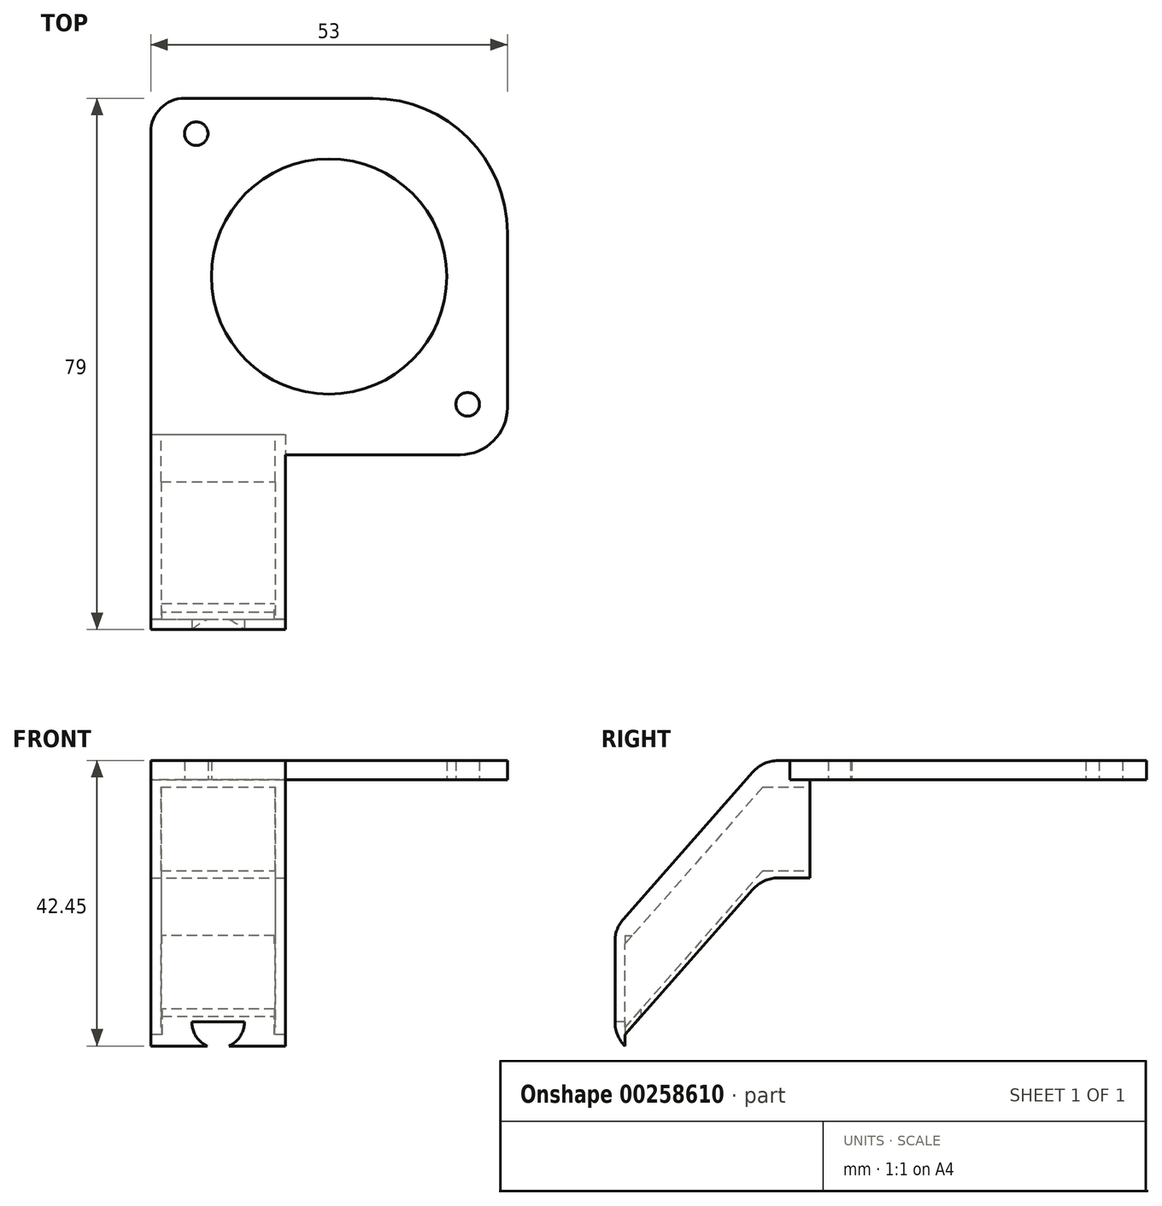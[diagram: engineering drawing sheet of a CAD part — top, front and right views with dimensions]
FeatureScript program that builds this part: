
annotation { "Feature Type Name" : "Feature", "Feature Type Description" : "" }
export const myFeature = defineFeature(function(context is Context, id is Id, definition is map)
    precondition{}
    {
        {
            var Q0;
            Q0=qCreatedBy(makeId("Top.planeOp"),FACE);
            var sketch = newSketch(context, id + "F0", { "sketchPlane" : qUnion([Q0])});
            skCircle(sketch, "E0", {"center": v(0, 0) * mm, "radius": 17.5 * mm});
            skLineSegment(sketch, "E1.bottom", {"start": v(19.5, -26.5) * mm, "end": v(-6.5, -26.5) * mm});
            skLineSegment(sketch, "E1.top", {"start": v(6.5, 26.5) * mm, "end": v(-21.5, 26.5) * mm});
            skLineSegment(sketch, "E1.left", {"start": v(26.5, -19.5) * mm, "end": v(26.5, 6.5) * mm});
            skLineSegment(sketch, "E1.right", {"start": v(-26.5, -26.5) * mm, "end": v(-26.5, 21.5) * mm});
            skCircle(sketch, "E2", {"center": v(-19.75, 21.25) * mm, "radius": 1.75 * mm});
            skCircle(sketch, "E3", {"center": v(20.6, -19.01) * mm, "radius": 1.75 * mm});
            skPoint(sketch, "E4.visualSharp", {"position": v(-26.5, 26.5) * mm});
            skArc(sketch, "E4.filletArc", {"start": v(-21.5, 26.5) * mm, "mid": v(-25.04, 25.04) * mm, "end": v(-26.5, 21.5) * mm});
            skPoint(sketch, "E5.visualSharp", {"position": v(26.5, -26.5) * mm});
            skArc(sketch, "E5.filletArc", {"start": v(19.5, -26.5) * mm, "mid": v(24.45, -24.45) * mm, "end": v(26.5, -19.5) * mm});
            skPoint(sketch, "E6.visualSharp", {"position": v(26.5, 26.5) * mm});
            skArc(sketch, "E6.filletArc", {"start": v(26.5, 6.5) * mm, "mid": v(20.64, 20.64) * mm, "end": v(6.5, 26.5) * mm});
            skLineSegment(sketch, "E7.top", {"start": v(-26.5, -30.5) * mm, "end": v(-6.5, -30.5) * mm});
            skLineSegment(sketch, "E7.left", {"start": v(-26.5, -26.5) * mm, "end": v(-26.5, -30.5) * mm});
            skLineSegment(sketch, "E7.right", {"start": v(-6.5, -26.5) * mm, "end": v(-6.5, -30.5) * mm});
            skSolve(sketch);
        }
        {
            var Q0;
            Q0=makeQuery(id+"F0.imprint","IMPRINT",FACE,{"disambiguationData":[TD([[makeQuery(id+"F0.imprint","IMPRINT",EDGE,{"derivedFrom":sQuery(id+"F0.wireOp",EDGE,"E0")}),-1.0]])]});
            extrude(context, id + "F1", {"entities" : qUnion([Q0]), "depth" : 2.85 * mm});
        }
        {
            var Q0;
            Q0=makeQuery(id+"F1.opExtrude","CAP_FACE",FACE,{"disambiguationData":[OSD([sQuery(id+"F0.wireOp",EDGE,"E0"),sQuery(id+"F0.wireOp",EDGE,"E1.bottom"),sQuery(id+"F0.wireOp",EDGE,"E1.top"),sQuery(id+"F0.wireOp",EDGE,"E1.left"),sQuery(id+"F0.wireOp",EDGE,"E1.right"),sQuery(id+"F0.wireOp",EDGE,"E2"),sQuery(id+"F0.wireOp",EDGE,"E3"),sQuery(id+"F0.wireOp",EDGE,"E4.filletArc"),sQuery(id+"F0.wireOp",EDGE,"E5.filletArc"),sQuery(id+"F0.wireOp",EDGE,"E6.filletArc"),sQuery(id+"F0.wireOp",EDGE,"E7.top"),sQuery(id+"F0.wireOp",EDGE,"E7.left"),sQuery(id+"F0.wireOp",EDGE,"E7.right")])],"isStart":true});
            var sketch = newSketch(context, id + "F2", { "sketchPlane" : qUnion([Q0])});
            skLineSegment(sketch, "E8.bottom", {"start": v(-26.5, 30.5) * mm, "end": v(-6.5, 30.5) * mm});
            skLineSegment(sketch, "E8.top", {"start": v(-26.5, 26.5) * mm, "end": v(-6.5, 26.5) * mm});
            skLineSegment(sketch, "E8.left", {"start": v(-26.5, 30.5) * mm, "end": v(-26.5, 26.5) * mm});
            skLineSegment(sketch, "E8.right", {"start": v(-6.5, 30.5) * mm, "end": v(-6.5, 26.5) * mm});
            skSolve(sketch);
        }
        {
            var Q0;
            Q0=makeQuery(id+"F2.imprint","IMPRINT",FACE,{"disambiguationData":[TD([[makeQuery(id+"F2.imprint","IMPRINT",EDGE,{"derivedFrom":sQuery(id+"F2.wireOp",EDGE,"E8.bottom")}),-1.0]])]});
            extrude(context, id + "F3", {"entities" : qUnion([Q0]), "operationType" : NewBodyOperationType.ADD, "depth" : 14.6 * mm});
        }
        {
            var Q0;
            Q0=makeQuery(id+"F3.opExtrude","SWEPT_FACE",FACE,{"disambiguationData":[OSD([sQuery(id+"F2.wireOp",EDGE,"E8.top")])]});
            var sketch = newSketch(context, id + "F4", { "sketchPlane" : qUnion([Q0])});
            skLineSegment(sketch, "E9", {"start": v(26.5, -14.6) * mm, "end": v(6.5, 0) * mm, "construction": true});
            skLineSegment(sketch, "E10", {"start": v(6.5, -14.6) * mm, "end": v(26.5, 0) * mm, "construction": true});
            skLineSegment(sketch, "E11.bottom", {"start": v(25, -13.5) * mm, "end": v(8, -13.5) * mm});
            skLineSegment(sketch, "E11.top", {"start": v(25, -1.1) * mm, "end": v(8, -1.1) * mm});
            skLineSegment(sketch, "E11.left", {"start": v(25, -13.5) * mm, "end": v(25, -1.1) * mm});
            skLineSegment(sketch, "E11.right", {"start": v(8, -13.5) * mm, "end": v(8, -1.1) * mm});
            skPoint(sketch, "E11.middle", {"position": v(16.5, -7.3) * mm});
            skSolve(sketch);
        }
        {
            var Q0;
            Q0=makeQuery(id+"F4.imprint","IMPRINT",FACE,{"disambiguationData":[TD([[makeQuery(id+"F4.imprint","IMPRINT",EDGE,{"derivedFrom":sQuery(id+"F4.wireOp",EDGE,"E11.bottom")}),-1.0]])]});
            extrude(context, id + "F5", {"entities" : qUnion([Q0]), "operationType" : NewBodyOperationType.REMOVE, "oppositeDirection" : true, "depth" : 25 * mm});
        }
        {
            var Q0;
            Q0=makeQuery(id+"F3.boolean.opBoolean","MERGE",FACE,{"derivedFrom":[makeQuery(id+"F1.opExtrude","SWEPT_FACE",FACE,{"disambiguationData":[OSD([sQuery(id+"F0.wireOp",EDGE,"E7.right")])]}),makeQuery(id+"F3.opExtrude","SWEPT_FACE",FACE,{"disambiguationData":[OSD([sQuery(id+"F2.wireOp",EDGE,"E8.right")])]})]});
            cPlane(context, id + "F6", {"entities" : qUnion([Q0]), "cplaneType" : CPlaneType.OFFSET, "offset" : 10 * mm, "oppositeDirection" : true, "width" : 150 * mm, "height" : 150 * mm});
        }
        {
            var Q0;
            Q0=qCreatedBy(id+"F6.planeOp",FACE);
            var sketch = newSketch(context, id + "F7", { "sketchPlane" : qUnion([Q0])});
            skLineSegment(sketch, "E12", {"start": v(-30.58, -0.14) * mm, "end": v(-52.58, -0.14) * mm, "construction": true});
            skLineSegment(sketch, "E13", {"start": v(-52.58, -0.14) * mm, "end": v(-52.58, -25.14) * mm, "construction": true});
            skLineSegment(sketch, "E14", {"start": v(-30.58, -0.14) * mm, "end": v(-52.58, -25.14) * mm});
            skSolve(sketch);
        }
        {
            var Q0;
            Q0=makeQuery(id+"F3.boolean.opBoolean","MERGE",FACE,{"derivedFrom":[makeQuery(id+"F1.opExtrude","SWEPT_FACE",FACE,{"disambiguationData":[OSD([sQuery(id+"F0.wireOp",EDGE,"E7.top")])]}),makeQuery(id+"F3.opExtrude","SWEPT_FACE",FACE,{"disambiguationData":[OSD([sQuery(id+"F2.wireOp",EDGE,"E8.bottom")])]})]});
            var Q1;
            Q1=sQuery(id+"F7.wireOp",EDGE,"E14");
            sweep(context, id + "F8", {"operationType" : NewBodyOperationType.ADD, "profiles" : qUnion([Q0]), "path" : qUnion([Q1])});
        }
        {
            var Q0;
            Q0=makeQuery(id+"F8.opSweep","CAP_FACE",FACE,{"disambiguationData":[OSD([sQuery(id+"F0.wireOp",EDGE,"E7.top"),sQuery(id+"F2.wireOp",EDGE,"E8.bottom"),sQuery(id+"F7.wireOp",VERTEX,"E14.end")])],"isStart":false});
            var sketch = newSketch(context, id + "F9", { "sketchPlane" : qUnion([Q0])});
            skLineSegment(sketch, "E15.bottom", {"start": v(-26.5, -22.15) * mm, "end": v(-6.5, -22.15) * mm});
            skLineSegment(sketch, "E15.top", {"start": v(-26.5, -39.6) * mm, "end": v(-6.5, -39.6) * mm});
            skLineSegment(sketch, "E15.left", {"start": v(-26.5, -22.15) * mm, "end": v(-26.5, -39.6) * mm});
            skLineSegment(sketch, "E15.right", {"start": v(-6.5, -22.15) * mm, "end": v(-6.5, -39.6) * mm});
            skSolve(sketch);
        }
        {
            var Q0;
            Q0 = qSketchRegion(id + "F9", true);
            extrude(context, id + "F10", {"entities" : qUnion([Q0]), "operationType" : NewBodyOperationType.ADD, "oppositeDirection" : true, "depth" : 1.5 * mm});
        }
        {
            var Q0;
            Q0=makeQuery(id+"F10.opExtrude","SWEPT_FACE",FACE,{"disambiguationData":[OSD([sQuery(id+"F9.wireOp",EDGE,"E15.top")])]});
            var sketch = newSketch(context, id + "F11", { "sketchPlane" : qUnion([Q0])});
            skLineSegment(sketch, "E16.bottom", {"start": v(-24.86, 51) * mm, "end": v(-8.14, 51) * mm});
            skLineSegment(sketch, "E16.top", {"start": v(-24.86, 48.63) * mm, "end": v(-8.14, 48.63) * mm});
            skLineSegment(sketch, "E16.left", {"start": v(-24.86, 51) * mm, "end": v(-24.86, 48.63) * mm});
            skLineSegment(sketch, "E16.right", {"start": v(-8.14, 51) * mm, "end": v(-8.14, 48.63) * mm});
            skSolve(sketch);
        }
        {
            var Q0;
            Q0=makeQuery(id+"F11.imprint","IMPRINT",FACE,{"disambiguationData":[TD([[makeQuery(id+"F11.imprint","IMPRINT",EDGE,{"derivedFrom":sQuery(id+"F11.wireOp",EDGE,"E16.bottom")}),-1.0]])]});
            extrude(context, id + "F12", {"entities" : qUnion([Q0]), "operationType" : NewBodyOperationType.REMOVE, "oppositeDirection" : true, "depth" : 16.4 * mm});
        }
        {
            var Q0;
            Q0=makeQuery(id+"F8.opSweep","CAP_EDGE",EDGE,{"disambiguationData":[OSD([sQuery(id+"F0.wireOp",EDGE,"E7.top"),sQuery(id+"F7.wireOp",VERTEX,"E14.end")])],"isStart":false});
            var Q1;
            {var subQ0=sQuery(id+"F0.wireOp",EDGE,"E7.top");Q1=makeQuery(id+"F8.boolean.opBoolean","MERGE",EDGE,{"derivedFrom":[makeQuery(id+"F1.opExtrude","CAP_EDGE",EDGE,{"disambiguationData":[OSD([subQ0])],"isStart":false}),makeQuery(id+"F8.opSweep","CAP_EDGE",EDGE,{"disambiguationData":[OSD([subQ0,sQuery(id+"F7.wireOp",VERTEX,"E14.start")])],"isStart":true})]});}
            var Q2;
            {var subQ0=sQuery(id+"F2.wireOp",EDGE,"E8.bottom");Q2=makeQuery(id+"F8.boolean.opBoolean","MERGE",EDGE,{"derivedFrom":[makeQuery(id+"F3.opExtrude","CAP_EDGE",EDGE,{"disambiguationData":[OSD([subQ0])],"isStart":false}),makeQuery(id+"F8.opSweep","CAP_EDGE",EDGE,{"disambiguationData":[OSD([subQ0,sQuery(id+"F7.wireOp",VERTEX,"E14.start")])],"isStart":true})]});}
            var Q3;
            Q3=makeQuery(id+"F10.boolean.opBoolean","MERGE",EDGE,{"derivedFrom":[makeQuery(id+"F8.opSweep","CAP_EDGE",EDGE,{"disambiguationData":[OSD([sQuery(id+"F2.wireOp",EDGE,"E8.bottom"),sQuery(id+"F7.wireOp",VERTEX,"E14.end")])],"isStart":false}),makeQuery(id+"F10.opExtrude","CAP_EDGE",EDGE,{"disambiguationData":[OSD([sQuery(id+"F9.wireOp",EDGE,"E15.top")])],"isStart":true})]});
            fillet(context, id + "F13", {"entities" : qUnion([Q0, Q1, Q2, Q3]), "radius" : 5 * mm, "tangentPropagation" : true, "allowEdgeOverflow" : false});
        }
        {
            var Q0;
            Q0=makeQuery(id+"F4.imprint","IMPRINT",FACE,{"disambiguationData":[TD([[makeQuery(id+"F4.imprint","IMPRINT",EDGE,{"derivedFrom":sQuery(id+"F4.wireOp",EDGE,"E11.bottom")}),1.0]])]});
            extrude(context, id + "F14", {"entities" : qUnion([Q0]), "operationType" : NewBodyOperationType.ADD, "depth" : 3 * mm});
        }
        {
            var Q0;
            Q0=makeQuery(id+"F10.boolean.opBoolean","MERGE",FACE,{"derivedFrom":[makeQuery(id+"F8.opSweep","CAP_FACE",FACE,{"disambiguationData":[OSD([sQuery(id+"F0.wireOp",EDGE,"E7.top"),sQuery(id+"F2.wireOp",EDGE,"E8.bottom"),sQuery(id+"F7.wireOp",VERTEX,"E14.end")])],"isStart":false}),makeQuery(id+"F10.opExtrude","CAP_FACE",FACE,{"disambiguationData":[OSD([sQuery(id+"F9.wireOp",EDGE,"E15.bottom"),sQuery(id+"F9.wireOp",EDGE,"E15.top"),sQuery(id+"F9.wireOp",EDGE,"E15.left"),sQuery(id+"F9.wireOp",EDGE,"E15.right")])],"isStart":true})]});
            var sketch = newSketch(context, id + "F15", { "sketchPlane" : qUnion([Q0])});
            skArc(sketch, "E17", {"start": v(-20.42, -36.03) * mm, "mid": v(-16.5, -39.95) * mm, "end": v(-12.58, -36.03) * mm});
            skLineSegment(sketch, "E18", {"start": v(-20.42, -36.03) * mm, "end": v(-12.58, -36.03) * mm});
            skSolve(sketch);
        }
        {
            var Q0;
            Q0=makeQuery(id+"F15.imprint","IMPRINT",FACE,{"disambiguationData":[TD([[makeQuery(id+"F15.imprint","IMPRINT",EDGE,{"derivedFrom":sQuery(id+"F15.wireOp",EDGE,"E17")}),1.0]])]});
            extrude(context, id + "F16", {"entities" : qUnion([Q0]), "operationType" : NewBodyOperationType.REMOVE, "oppositeDirection" : true, "depth" : 25 * mm});
        }
    });
